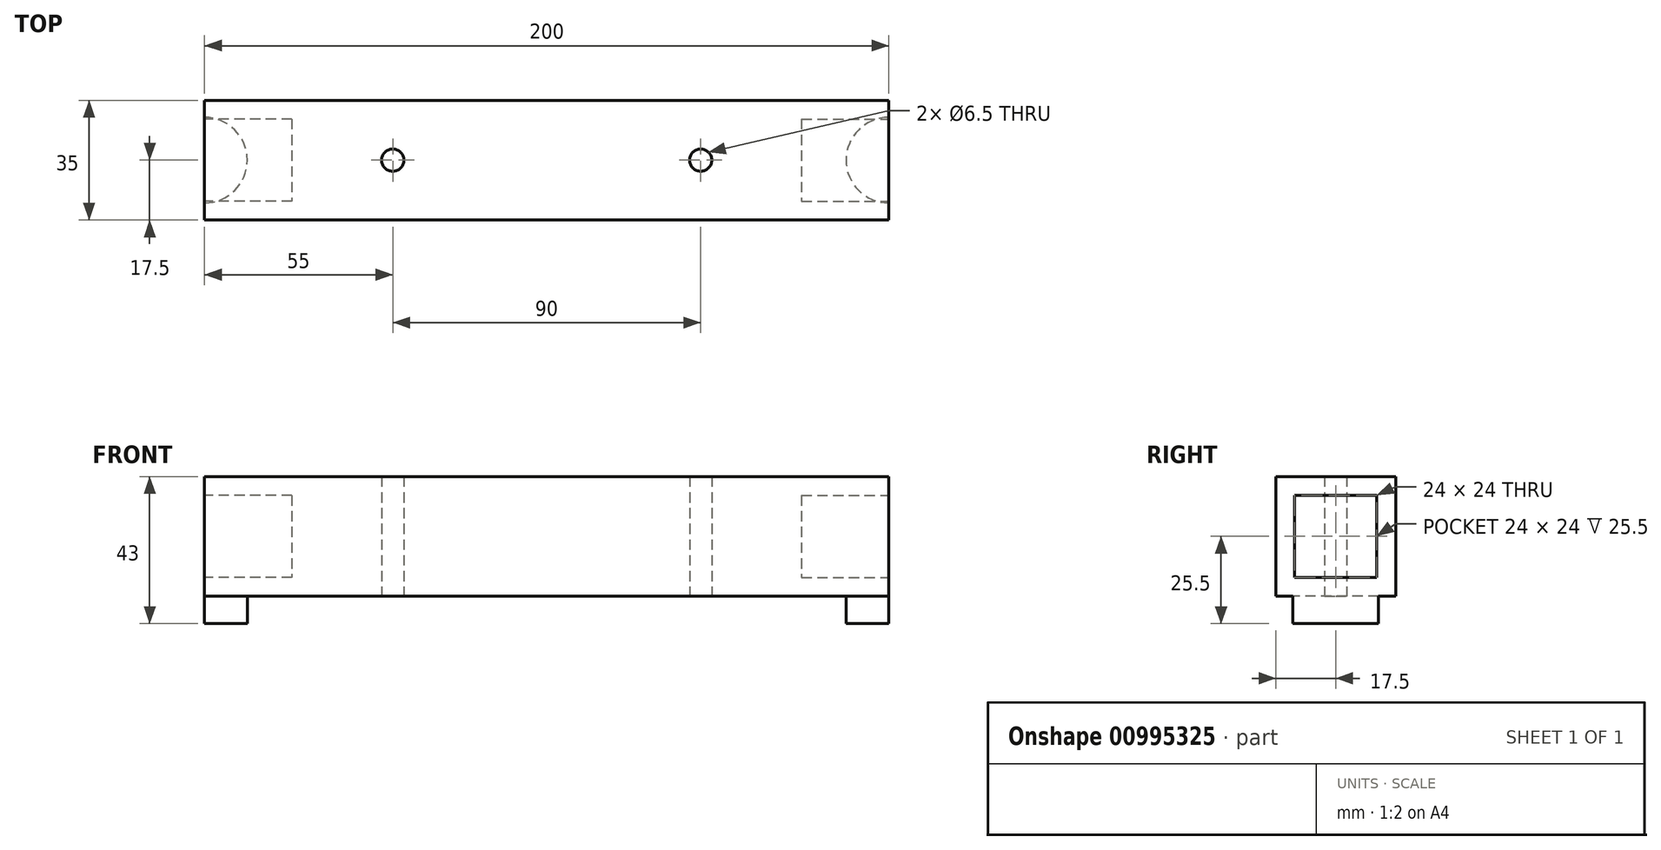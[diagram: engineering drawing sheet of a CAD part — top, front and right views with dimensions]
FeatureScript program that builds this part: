
annotation { "Feature Type Name" : "Feature", "Feature Type Description" : "" }
export const myFeature = defineFeature(function(context is Context, id is Id, definition is map)
    precondition{}
    {
        {
            var Q0;
            Q0=qCreatedBy(makeId("Top.planeOp"),FACE);
            var sketch = newSketch(context, id + "F0", { "sketchPlane" : qUnion([Q0])});
            skLineSegment(sketch, "E0.bottom", {"start": v(100, 17.5) * mm, "end": v(-100, 17.5) * mm});
            skLineSegment(sketch, "E0.top", {"start": v(100, -17.5) * mm, "end": v(-100, -17.5) * mm});
            skLineSegment(sketch, "E0.left", {"start": v(100, 17.5) * mm, "end": v(100, -17.5) * mm});
            skLineSegment(sketch, "E0.right", {"start": v(-100, 17.5) * mm, "end": v(-100, -17.5) * mm});
            skPoint(sketch, "E0.middle", {"position": v(0, 0) * mm});
            skSolve(sketch);
        }
        {
            var Q0;
            Q0=makeQuery(id+"F0.imprint","IMPRINT",FACE,{"disambiguationData":[TD([[makeQuery(id+"F0.imprint","IMPRINT",EDGE,{"derivedFrom":sQuery(id+"F0.wireOp",EDGE,"E0.bottom")}),1.0]])]});
            extrude(context, id + "F1", {"entities" : qUnion([Q0]), "depth" : 35 * mm, "offsetDistance" : 25 * mm});
        }
        {
            var Q0;
            Q0=makeQuery(id+"F1.opExtrude","SWEPT_FACE",FACE,{"disambiguationData":[OSD([sQuery(id+"F0.wireOp",EDGE,"E0.left")])]});
            var sketch = newSketch(context, id + "F2", { "sketchPlane" : qUnion([Q0])});
            skLineSegment(sketch, "E1.0", {"start": v(12, 29.5) * mm, "end": v(-12, 29.5) * mm});
            skLineSegment(sketch, "E1.1", {"start": v(12, 29.5) * mm, "end": v(12, 5.5) * mm});
            skLineSegment(sketch, "E2.0", {"start": v(12, 5.5) * mm, "end": v(-12, 5.5) * mm});
            skLineSegment(sketch, "E2.1", {"start": v(-12, 29.5) * mm, "end": v(-12, 5.5) * mm});
            skSolve(sketch);
        }
        {
            var Q0;
            Q0=makeQuery(id+"F2.imprint","IMPRINT",FACE,{"disambiguationData":[TD([[makeQuery(id+"F2.imprint","IMPRINT",EDGE,{"derivedFrom":sQuery(id+"F2.wireOp",EDGE,"E1.0")}),1.0]])]});
            extrude(context, id + "F3", {"entities" : qUnion([Q0]), "operationType" : NewBodyOperationType.REMOVE, "oppositeDirection" : true, "depth" : 25.5 * mm, "offsetDistance" : 25 * mm});
        }
        {
            var Q0;
            Q0=makeQuery(id+"F1.opExtrude","SWEPT_FACE",FACE,{"disambiguationData":[OSD([sQuery(id+"F0.wireOp",EDGE,"E0.right")])]});
            var sketch = newSketch(context, id + "F4", { "sketchPlane" : qUnion([Q0])});
            skLineSegment(sketch, "E3.0", {"start": v(-12, 5.5) * mm, "end": v(12, 5.5) * mm});
            skLineSegment(sketch, "E3.1", {"start": v(-12, 29.5) * mm, "end": v(-12, 5.5) * mm});
            skLineSegment(sketch, "E4.0", {"start": v(12, 29.5) * mm, "end": v(12, 5.5) * mm});
            skLineSegment(sketch, "E4.1", {"start": v(-12, 29.5) * mm, "end": v(12, 29.5) * mm});
            skSolve(sketch);
        }
        {
            var Q0;
            Q0=makeQuery(id+"F4.imprint","IMPRINT",FACE,{"disambiguationData":[TD([[makeQuery(id+"F4.imprint","IMPRINT",EDGE,{"derivedFrom":sQuery(id+"F4.wireOp",EDGE,"E3.0")}),1.0]])]});
            extrude(context, id + "F5", {"entities" : qUnion([Q0]), "operationType" : NewBodyOperationType.REMOVE, "oppositeDirection" : true, "depth" : 25.5 * mm, "offsetDistance" : 25 * mm});
        }
        {
            var Q0;
            Q0=makeQuery(id+"F1.opExtrude","CAP_FACE",FACE,{"disambiguationData":[OSD([sQuery(id+"F0.wireOp",EDGE,"E0.bottom"),sQuery(id+"F0.wireOp",EDGE,"E0.top"),sQuery(id+"F0.wireOp",EDGE,"E0.left"),sQuery(id+"F0.wireOp",EDGE,"E0.right")])],"isStart":true});
            var sketch = newSketch(context, id + "F6", { "sketchPlane" : qUnion([Q0])});
            skPoint(sketch, "E5", {"position": v(100, 0) * mm});
            skPoint(sketch, "E6", {"position": v(45, 0) * mm});
            skPoint(sketch, "E7", {"position": v(-100, 0) * mm});
            skPoint(sketch, "E8", {"position": v(-45, 0) * mm});
            skSolve(sketch);
        }
        {
            var Q0;
            Q0=sQuery(id+"F6.wireOp",VERTEX,"E8");
            var Q1;
            Q1=sQuery(id+"F6.wireOp",VERTEX,"E6");
            var Q2;
            Q2=makeQuery(id+"F1.opExtrude","SWEPT_BODY",BODY,{"disambiguationData":[OSD([sQuery(id+"F0.wireOp",EDGE,"E0.bottom"),sQuery(id+"F0.wireOp",EDGE,"E0.top"),sQuery(id+"F0.wireOp",EDGE,"E0.left"),sQuery(id+"F0.wireOp",EDGE,"E0.right")])]});
            hole(context, id + "F7", {"style" : HoleStyle.SIMPLE, "endStyle" : HoleEndStyle.BLIND, "holeDiameter" : 6.5 * mm, "majorDiameter" : 5 * mm, "holeDepth" : 35 * mm, "isTappedThrough" : true, "tappedDepth" : 12 * mm, "tapClearance" : 3, "locations" : qUnion([Q0, Q1]), "scope" : qUnion([Q2])});
        }
        {
            var Q0;
            Q0=makeQuery(id+"F1.opExtrude","CAP_FACE",FACE,{"disambiguationData":[OSD([sQuery(id+"F0.wireOp",EDGE,"E0.bottom"),sQuery(id+"F0.wireOp",EDGE,"E0.top"),sQuery(id+"F0.wireOp",EDGE,"E0.left"),sQuery(id+"F0.wireOp",EDGE,"E0.right")])],"isStart":true});
            var sketch = newSketch(context, id + "F8", { "sketchPlane" : qUnion([Q0])});
            skCircle(sketch, "E9", {"center": v(100, 0) * mm, "radius": 12.5 * mm});
            skCircle(sketch, "E10", {"center": v(-100, 0) * mm, "radius": 12.5 * mm});
            skSolve(sketch);
        }
        {
            var Q0;
            {var subQ0=sQuery(id+"F8.wireOp",EDGE,"E9");var subQ1=makeQuery(id+"F1.opExtrude","CAP_EDGE",EDGE,{"disambiguationData":[OSD([sQuery(id+"F0.wireOp",EDGE,"E0.left")])],"isStart":true});var subQ2=makeQuery(id+"F8.imprint","INTERSECT",VERTEX,{"disambiguationData":[OD(0.0)],"derivedFrom":[subQ1,subQ0]});Q0=makeQuery(id+"F8.imprint","IMPRINT",FACE,{"disambiguationData":[TD([[makeQuery(id+"F8.imprint","IMPRINT",EDGE,{"disambiguationData":[TD([[subQ2,1.0]])],"derivedFrom":subQ0}),1.0]])]});}
            var Q1;
            {var subQ0=sQuery(id+"F8.wireOp",EDGE,"E10");var subQ1=makeQuery(id+"F1.opExtrude","CAP_EDGE",EDGE,{"disambiguationData":[OSD([sQuery(id+"F0.wireOp",EDGE,"E0.right")])],"isStart":true});var subQ2=makeQuery(id+"F8.imprint","INTERSECT",VERTEX,{"disambiguationData":[OD(0.0)],"derivedFrom":[subQ1,subQ0]});Q1=makeQuery(id+"F8.imprint","IMPRINT",FACE,{"disambiguationData":[TD([[makeQuery(id+"F8.imprint","IMPRINT",EDGE,{"disambiguationData":[TD([[subQ2,-1.0]])],"derivedFrom":subQ0}),1.0]])]});}
            var Q2;
            Q2=sQuery(id+"F8.wireOp",EDGE,"E9");
            extrude(context, id + "F9", {"entities" : qUnion([Q0, Q1]), "operationType" : NewBodyOperationType.ADD, "surfaceEntities" : qUnion([Q2]), "depth" : 8 * mm, "offsetDistance" : 25 * mm});
        }
    });
